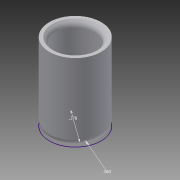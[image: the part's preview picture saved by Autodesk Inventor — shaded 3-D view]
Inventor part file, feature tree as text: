
AUTODESK INVENTOR PART (.ipt)
format: ipt  version: 2014 (Build 180170000, 170)  size: 111,104 bytes
history: native  units: in
note: dims shown in document units (in); Inventor stores cm internally (conversion verified against a paired STEP export)
features: extrude x2, fillet x2, sketch x1, chamfer x1
ambient origin geometry x8: Origin, YZ Plane, XZ Plane, XY Plane, X Axis, Y Axis, Z Axis, Center Point
bodies: Solid1 (feature_tree)
feature tree (6):
  sketch  "Sketch1"  dims[d0=0.378in d1=0.0625in d2=0.75in d3=0.0in d4=0.125in d5=0.0in d6=0.0625in d7=0.0312in d8=0.125in d9=45.0deg d10=0.0625in]
  extrude  "Extrusion1"  Depth=0.0625in
  extrude  "Extrusion2"  Depth=0.75in TaperAngle=0.0deg
  fillet  "Fillet1"  Radius=0.125in
  chamfer  "Chamfer1"  Distance=0.0625in
  fillet  "Fillet2"  Radius=0.125in
